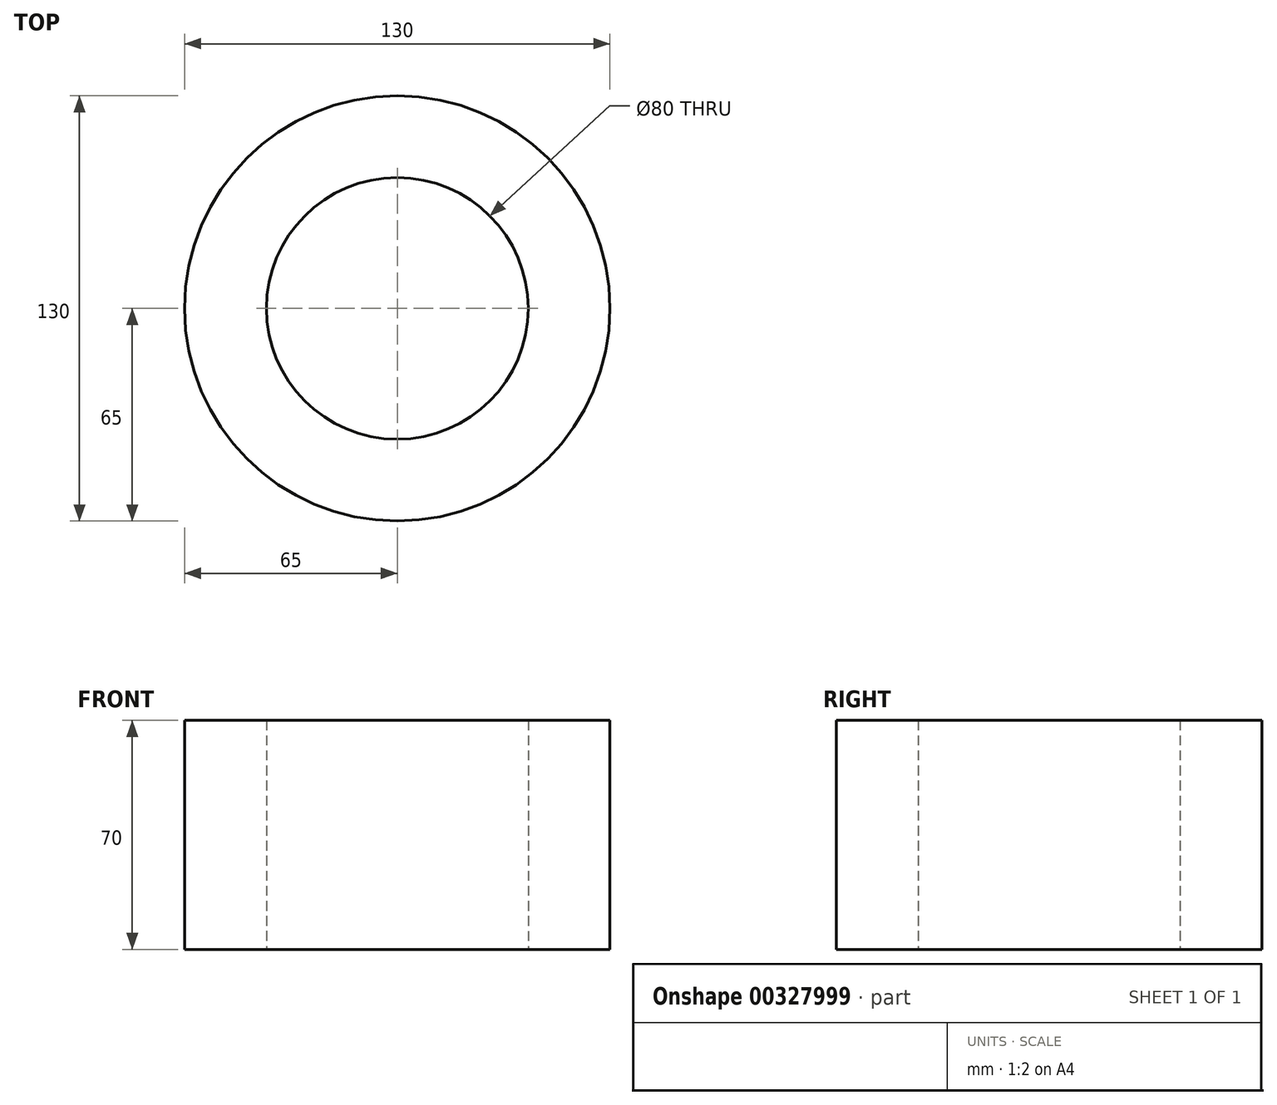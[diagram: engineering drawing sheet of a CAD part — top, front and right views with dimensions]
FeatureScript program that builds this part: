
annotation { "Feature Type Name" : "Feature", "Feature Type Description" : "" }
export const myFeature = defineFeature(function(context is Context, id is Id, definition is map)
    precondition{}
    {
        {
            var Q0;
            Q0=qCreatedBy(makeId("Top.planeOp"),FACE);
            var sketch = newSketch(context, id + "F0", { "sketchPlane" : qUnion([Q0])});
            skCircle(sketch, "E0", {"center": v(0, 0) * mm, "radius": 40 * mm});
            skCircle(sketch, "E1", {"center": v(0, 0) * mm, "radius": 65 * mm});
            skSolve(sketch);
        }
        {
            var Q0;
            Q0=makeQuery(id+"F0.imprint","IMPRINT",FACE,{"disambiguationData":[TD([[makeQuery(id+"F0.imprint","IMPRINT",EDGE,{"derivedFrom":sQuery(id+"F0.wireOp",EDGE,"E0")}),-1.0]])]});
            extrude(context, id + "F1", {"entities" : qUnion([Q0]), "endBound" : BoundingType.SYMMETRIC, "depth" : 70 * mm});
        }
    });
